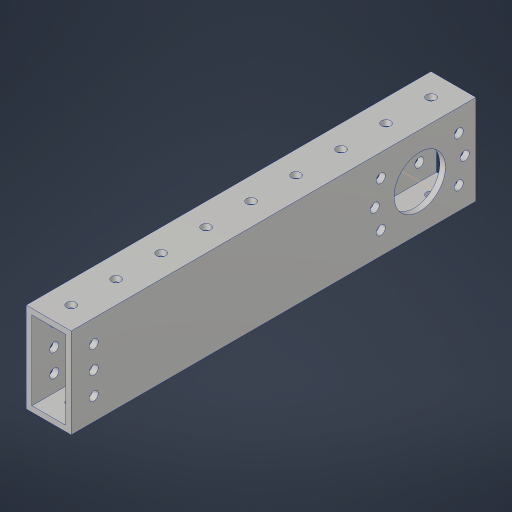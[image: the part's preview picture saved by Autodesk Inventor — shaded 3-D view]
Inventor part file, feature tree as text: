
AUTODESK INVENTOR PART (.ipt)
format: ipt  version: 2023.4 (Build 274418000, 418)  size: 273,920 bytes
history: native  units: in
note: dims shown in document units (in); Inventor stores cm internally (conversion verified against a paired STEP export)
features: sketch x6, hole x5, projected_geometry x5, extrude x4, pattern_linear x1, other x1
ambient origin geometry x8: Origin, YZ Plane, XZ Plane, XY Plane, X Axis, Y Axis, Z Axis, Center Point
bodies: Solid1 (feature_tree)
feature tree (22):
  extrude  "Extrusion1"  Depth=1.125in
  extrude  "Extrusion3"  TaperAngle=0.0deg  [1 undecoded]
  extrude  "Extrusion4"  TaperAngle=45.0deg  [1 undecoded]
  hole  "Hole1"  [1 undecoded]
  pattern_linear  "Rectangular Pattern1"  Spacing1=0.0in  [1 undecoded]
  extrude  "Extrusion5"  Depth=1.0in
  hole  "Hole2"  [1 undecoded]
  sketch  "Sketch8"  dims[d29=45.0deg d30=0.0in d31=0.0in d32=0.5in d33=0.5in d34=0.5in d35=0.201in d36=0.75in d37=0.375in d38=0.25in d39=0.5635in d40=1.0in d41=0.8108in d42=1.875in d43=2.0in d44=4.0in d45=6.0in d46=1.25in d47=2.3622in d49=360.0deg d51=4.7244in d53=360.0deg d55=0.177in d56=0.75in d57=0.332in d58=0.25in d59=0.5635in d60=1.0in d61=0.8108in d62=0.201in d63=0.75in d64=0.385in d65=0.25in d66=0.5635in d67=1.0in d68=0.8108in d69=1.14in d70=0.75in d71=0.375in d72=0.25in d73=0.5635in d74=1.0in d75=0.8108in]
  hole  "Hole3"  [1 undecoded]
  hole  "Hole4"  [1 undecoded]
  hole  "Hole5"  [1 undecoded]
  other  "Work Axis1"
  sketch  "Sketch3"  dims[d4=0.0in d8=1.125in]
  sketch  "Sketch4"  dims[d9=1.0in d10=0.0in d11=0.0in]
  projected_geometry  "Projected Loop2"
  sketch  "Sketch5"  dims[d14=0.0in d15=0.0in d17=45.0deg]
  sketch  "Sketch6"  dims[d18=0.5in]
  sketch  "Sketch7"  dims[d19=0.201in d20=0.75in d21=0.385in d22=0.25in d23=0.5635in d24=1.0in d25=0.8108in d26=3.5433in d28=1.0in]
  projected_geometry  "Project Cut Edges1"
  projected_geometry  "Project Cut Edges2"
  projected_geometry  "Project Cut Edges3"
  projected_geometry  "Project Cut Edges4"
note: 8 required parameter values undecoded (feature->parameter linkage not recoverable at this tier; creation-order binding heuristic only, values carry confidence <= 0.55)
